# Revit family: Basketball_Backstop-Outdoor-Ultimate_Fixed_Height-IPIbyBison-BA873-74
name_source: partatom
category: Specialty Equipment
units: mm (PartAtom-declared; Revit-internal decimal feet)

## family parameters
Always vertical = Yes
Cut with Voids When Loaded = No
Enable Cutting in Views = No
Maintain Annotation Orientation = No
OmniClass Number = 23.40.50.34.14
OmniClass Title = Gymnasium Equipment
Part Type = Normal
Room Calculation Point = No
Round Connector Dimension = Use Diameter
Shared = No
Work Plane-Based = No

## types (3) — shared parameters
Backboard Height = 3' - 6"
Backboard Length = 6' - 0"
Basket Netting = Finish - IPI by Bison - White Netting
CAD Details = https://www.arcat.com
Default Elevation = 0' - 0"
Description = Outdoor Basketball Frame and Backboard Systems
Embedding Depth = 4' - 0"
Hoop Elevation = 10' - 0"
Hoop Finish = Powder Coat - Playground Orange
Keynote = 11 66 00
Manufacturer = IPI by Bison
Padding = Padding - Black
Post Height = 8' - 4"
Post Material = Steel - Galvanized - Hot Dipped
Post Square Width = 0' - 6"
Product Page URL = https://www.arcat.com
Specification = https://www.arcat.com
URL = https://ipibybison.com

## per-type parameters (varying)
| type | Backboard BA42RG | Backboard BA472PC | Backboard Finish | Basket Type |
| BA874-BK | No | Yes | Steel - Galvanized - Perforated | BA39U |
| BA873U-BK | Yes | No | Powder Coat - White | BA32 |
| BK873-BK | Yes | No | Powder Coat - White | BA32 |

note: column(s) folded — value = type name in every type: Model

## geometry (parser evidence)
native form markers: Sweep x6
no freeform markers — native parametric forms only
